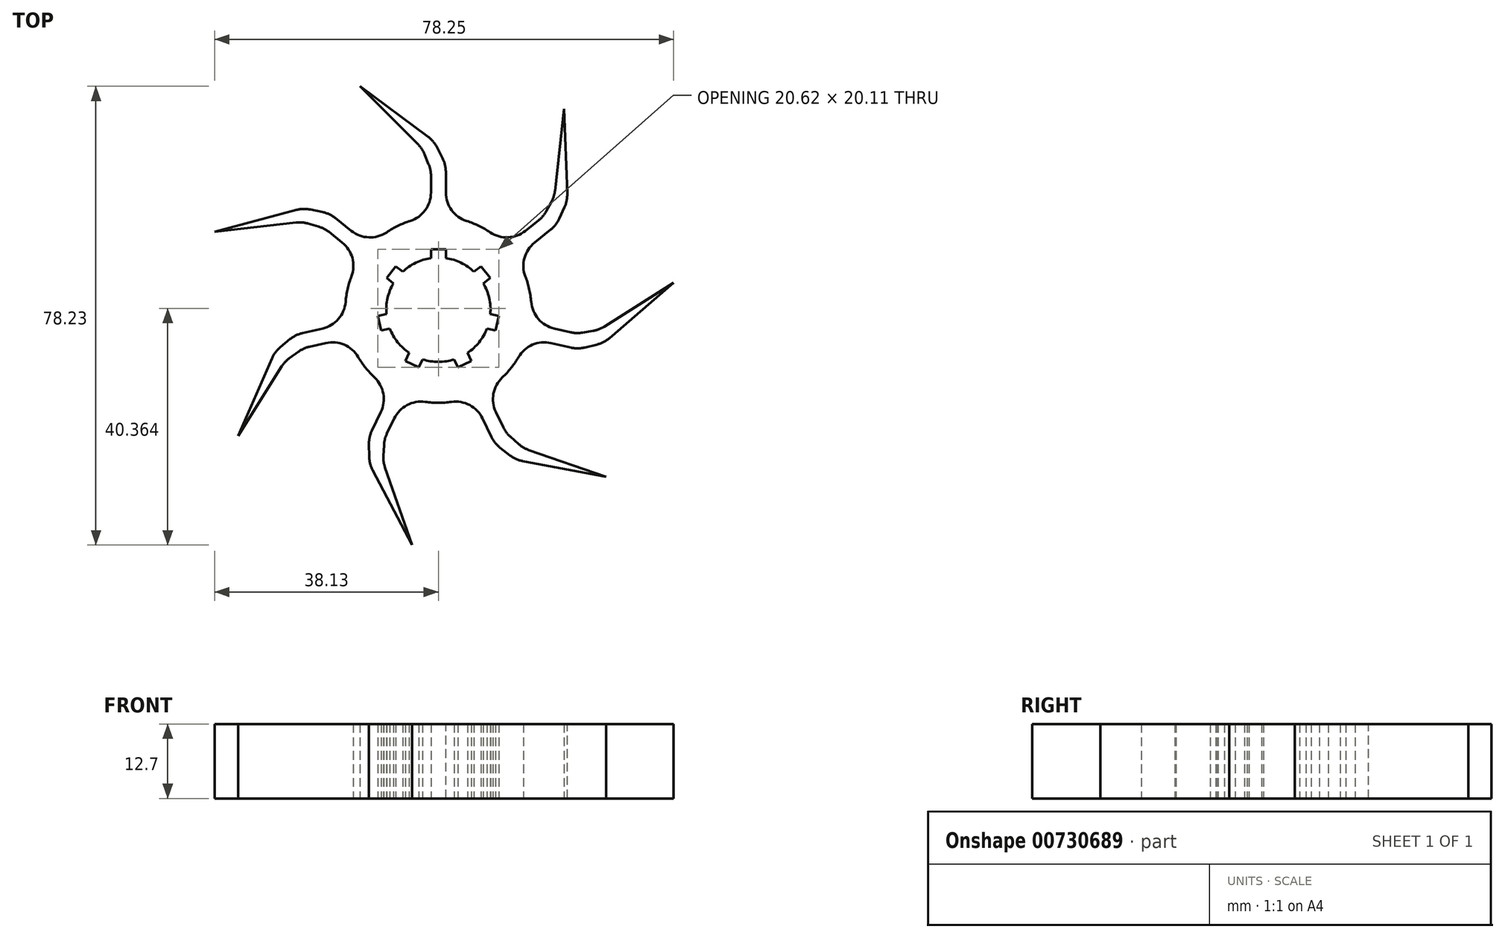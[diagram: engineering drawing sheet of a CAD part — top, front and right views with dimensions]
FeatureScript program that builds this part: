
annotation { "Feature Type Name" : "Feature", "Feature Type Description" : "" }
export const myFeature = defineFeature(function(context is Context, id is Id, definition is map)
    precondition{}
    {
        {
            var Q0;
            Q0=qCreatedBy(makeId("Top.planeOp"),FACE);
            var sketch = newSketch(context, id + "F0", { "sketchPlane" : qUnion([Q0])});
            skCircle(sketch, "E0", {"center": v(0, 0) * mm, "radius": 8.9 * mm});
            skLineSegment(sketch, "E1", {"start": v(-1.27, 8.8) * mm, "end": v(-1.27, 10.29) * mm});
            skLineSegment(sketch, "E2", {"start": v(-1.27, 10.29) * mm, "end": v(1.27, 10.29) * mm});
            skLineSegment(sketch, "E3", {"start": v(1.27, 10.29) * mm, "end": v(1.27, 8.8) * mm});
            skLineSegment(sketch, "E4.1.0", {"start": v(-8.83, 5.42) * mm, "end": v(-7.25, 7.4) * mm});
            skLineSegment(sketch, "E4.1.1", {"start": v(-7.25, 7.4) * mm, "end": v(-6.09, 6.48) * mm});
            skLineSegment(sketch, "E4.1.2", {"start": v(-7.67, 4.5) * mm, "end": v(-8.83, 5.42) * mm});
            skLineSegment(sketch, "E4.2.0", {"start": v(-9.75, -3.53) * mm, "end": v(-10.31, -1.05) * mm});
            skLineSegment(sketch, "E4.2.1", {"start": v(-10.31, -1.05) * mm, "end": v(-8.86, -0.72) * mm});
            skLineSegment(sketch, "E4.2.2", {"start": v(-8.3, -3.2) * mm, "end": v(-9.75, -3.53) * mm});
            skLineSegment(sketch, "E4.3.0", {"start": v(-3.32, -9.82) * mm, "end": v(-5.6, -8.72) * mm});
            skLineSegment(sketch, "E4.3.1", {"start": v(-5.6, -8.72) * mm, "end": v(-4.96, -7.38) * mm});
            skLineSegment(sketch, "E4.3.2", {"start": v(-2.67, -8.48) * mm, "end": v(-3.32, -9.82) * mm});
            skLineSegment(sketch, "E4.4.0", {"start": v(5.6, -8.72) * mm, "end": v(3.32, -9.82) * mm});
            skLineSegment(sketch, "E4.4.1", {"start": v(3.32, -9.82) * mm, "end": v(2.67, -8.48) * mm});
            skLineSegment(sketch, "E4.4.2", {"start": v(4.96, -7.38) * mm, "end": v(5.6, -8.72) * mm});
            skLineSegment(sketch, "E4.5.0", {"start": v(10.31, -1.05) * mm, "end": v(9.75, -3.53) * mm});
            skLineSegment(sketch, "E4.5.1", {"start": v(9.75, -3.53) * mm, "end": v(8.3, -3.2) * mm});
            skLineSegment(sketch, "E4.5.2", {"start": v(8.86, -0.72) * mm, "end": v(10.31, -1.05) * mm});
            skLineSegment(sketch, "E4.6.0", {"start": v(7.25, 7.4) * mm, "end": v(8.83, 5.42) * mm});
            skLineSegment(sketch, "E4.6.1", {"start": v(8.83, 5.42) * mm, "end": v(7.67, 4.5) * mm});
            skLineSegment(sketch, "E4.6.2", {"start": v(6.09, 6.48) * mm, "end": v(7.25, 7.4) * mm});
            skSolve(sketch);
        }
        {
            var Q0;
            Q0=qCreatedBy(makeId("Top.planeOp"),FACE);
            var sketch = newSketch(context, id + "F1", { "sketchPlane" : qUnion([Q0])});
            skCircle(sketch, "E5", {"center": v(0, 0) * mm, "radius": 15.88 * mm});
            skLineSegment(sketch, "E6", {"start": v(-1.27, 15.82) * mm, "end": v(-1.27, 25.98) * mm});
            skLineSegment(sketch, "E7", {"start": v(1.27, 27.25) * mm, "end": v(1.27, 15.82) * mm});
            skLineSegment(sketch, "E8", {"start": v(1.27, 27.25) * mm, "end": v(-13.39, 38.1) * mm});
            skLineSegment(sketch, "E9", {"start": v(-13.39, 38.1) * mm, "end": v(-1.27, 25.98) * mm});
            skLineSegment(sketch, "E10.1.0", {"start": v(-20.52, 17.99) * mm, "end": v(-11.58, 10.86) * mm});
            skLineSegment(sketch, "E10.1.1", {"start": v(-13.16, 8.87) * mm, "end": v(-21.1, 15.2) * mm});
            skLineSegment(sketch, "E10.1.2", {"start": v(-38.13, 13.29) * mm, "end": v(-21.1, 15.2) * mm});
            skLineSegment(sketch, "E10.1.3", {"start": v(-20.52, 17.99) * mm, "end": v(-38.13, 13.29) * mm});
            skLineSegment(sketch, "E10.2.0", {"start": v(-26.85, -4.83) * mm, "end": v(-15.7, -2.28) * mm});
            skLineSegment(sketch, "E10.2.1", {"start": v(-15.14, -4.76) * mm, "end": v(-25.05, -7.02) * mm});
            skLineSegment(sketch, "E10.2.2", {"start": v(-34.17, -21.53) * mm, "end": v(-25.05, -7.02) * mm});
            skLineSegment(sketch, "E10.2.3", {"start": v(-26.85, -4.83) * mm, "end": v(-34.17, -21.53) * mm});
            skLineSegment(sketch, "E10.3.0", {"start": v(-12.97, -24) * mm, "end": v(-8.01, -13.7) * mm});
            skLineSegment(sketch, "E10.3.1", {"start": v(-5.72, -14.8) * mm, "end": v(-10.13, -23.96) * mm});
            skLineSegment(sketch, "E10.3.2", {"start": v(-4.47, -40.13) * mm, "end": v(-10.13, -23.96) * mm});
            skLineSegment(sketch, "E10.3.3", {"start": v(-12.97, -24) * mm, "end": v(-4.47, -40.13) * mm});
            skLineSegment(sketch, "E10.4.0", {"start": v(10.68, -25.1) * mm, "end": v(5.72, -14.8) * mm});
            skLineSegment(sketch, "E10.4.1", {"start": v(8.01, -13.7) * mm, "end": v(12.42, -22.86) * mm});
            skLineSegment(sketch, "E10.4.2", {"start": v(28.6, -28.52) * mm, "end": v(12.42, -22.86) * mm});
            skLineSegment(sketch, "E10.4.3", {"start": v(10.68, -25.1) * mm, "end": v(28.6, -28.52) * mm});
            skLineSegment(sketch, "E10.5.0", {"start": v(26.29, -7.3) * mm, "end": v(15.14, -4.76) * mm});
            skLineSegment(sketch, "E10.5.1", {"start": v(15.7, -2.28) * mm, "end": v(25.62, -4.54) * mm});
            skLineSegment(sketch, "E10.5.2", {"start": v(40.12, 4.57) * mm, "end": v(25.62, -4.54) * mm});
            skLineSegment(sketch, "E10.5.3", {"start": v(26.29, -7.3) * mm, "end": v(40.12, 4.57) * mm});
            skLineSegment(sketch, "E10.6.0", {"start": v(22.1, 16) * mm, "end": v(13.16, 8.87) * mm});
            skLineSegment(sketch, "E10.6.1", {"start": v(11.58, 10.86) * mm, "end": v(19.52, 17.2) * mm});
            skLineSegment(sketch, "E10.6.2", {"start": v(21.44, 34.22) * mm, "end": v(19.52, 17.2) * mm});
            skLineSegment(sketch, "E10.6.3", {"start": v(22.1, 16) * mm, "end": v(21.44, 34.22) * mm});
            skSolve(sketch);
        }
        {
            var Q0;
            {var subQ0=sQuery(id+"F1.wireOp",EDGE,"E5");var subQ8=makeQuery(id+"F1.imprint","INTERSECT",VERTEX,{"derivedFrom":[subQ0,sQuery(id+"F1.wireOp",EDGE,"E10.6.0")]});Q0=makeQuery(id+"F1.imprint","IMPRINT",FACE,{"disambiguationData":[TD([[makeQuery(id+"F1.imprint","IMPRINT",EDGE,{"disambiguationData":[TD([[subQ8,-1.0]])],"derivedFrom":subQ0}),1.0]])]});}
            var Q1;
            {var subQ0=sQuery(id+"F1.wireOp",EDGE,"E10.1.0");Q1=makeQuery(id+"F1.imprint","IMPRINT",FACE,{"disambiguationData":[TD([[makeQuery(id+"F1.imprint","IMPRINT",EDGE,{"derivedFrom":subQ0}),-1.0]])]});}
            var Q2;
            {var subQ1=sQuery(id+"F1.wireOp",EDGE,"E10.2.0");Q2=makeQuery(id+"F1.imprint","IMPRINT",FACE,{"disambiguationData":[TD([[makeQuery(id+"F1.imprint","IMPRINT",EDGE,{"derivedFrom":subQ1}),-1.0]])]});}
            var Q3;
            {var subQ1=sQuery(id+"F1.wireOp",EDGE,"E10.3.0");Q3=makeQuery(id+"F1.imprint","IMPRINT",FACE,{"disambiguationData":[TD([[makeQuery(id+"F1.imprint","IMPRINT",EDGE,{"derivedFrom":subQ1}),-1.0]])]});}
            var Q4;
            {var subQ0=sQuery(id+"F1.wireOp",EDGE,"E10.4.0");Q4=makeQuery(id+"F1.imprint","IMPRINT",FACE,{"disambiguationData":[TD([[makeQuery(id+"F1.imprint","IMPRINT",EDGE,{"derivedFrom":subQ0}),-1.0]])]});}
            var Q5;
            {var subQ1=sQuery(id+"F1.wireOp",EDGE,"E6");Q5=makeQuery(id+"F1.imprint","IMPRINT",FACE,{"disambiguationData":[TD([[makeQuery(id+"F1.imprint","IMPRINT",EDGE,{"derivedFrom":subQ1}),-1.0]])]});}
            var Q6;
            {var subQ1=sQuery(id+"F1.wireOp",EDGE,"E10.6.0");Q6=makeQuery(id+"F1.imprint","IMPRINT",FACE,{"disambiguationData":[TD([[makeQuery(id+"F1.imprint","IMPRINT",EDGE,{"derivedFrom":subQ1}),-1.0]])]});}
            var Q7;
            {var subQ1=sQuery(id+"F1.wireOp",EDGE,"E10.5.0");Q7=makeQuery(id+"F1.imprint","IMPRINT",FACE,{"disambiguationData":[TD([[makeQuery(id+"F1.imprint","IMPRINT",EDGE,{"derivedFrom":subQ1}),-1.0]])]});}
            extrude(context, id + "F2", {"entities" : qUnion([Q0, Q1, Q2, Q3, Q4, Q5, Q6, Q7]), "depth" : 12.7 * mm, "offsetDistance" : 25.4 * mm});
        }
        {
            var Q0;
            Q0 = qSketchRegion(id + "F0", true);
            extrude(context, id + "F3", {"entities" : qUnion([Q0]), "operationType" : NewBodyOperationType.REMOVE, "endBound" : BoundingType.THROUGH_ALL, "depth" : 25.4 * mm, "offsetDistance" : 25.4 * mm});
        }
        {
            var Q0;
            Q0=makeQuery(id+"F2.opExtrude","SWEPT_EDGE",EDGE,{"disambiguationData":[OSD([sQuery(id+"F1.wireOp",EDGE,"E10.1.0"),sQuery(id+"F1.wireOp",EDGE,"E10.1.3")])]});
            var Q1;
            Q1=makeQuery(id+"F2.opExtrude","SWEPT_EDGE",EDGE,{"disambiguationData":[OSD([sQuery(id+"F1.wireOp",EDGE,"E10.1.1"),sQuery(id+"F1.wireOp",EDGE,"E10.1.2")])]});
            var Q2;
            Q2=makeQuery(id+"F2.opExtrude","SWEPT_EDGE",EDGE,{"disambiguationData":[OSD([sQuery(id+"F1.wireOp",EDGE,"E6"),sQuery(id+"F1.wireOp",EDGE,"E9")])]});
            var Q3;
            Q3=makeQuery(id+"F2.opExtrude","SWEPT_EDGE",EDGE,{"disambiguationData":[OSD([sQuery(id+"F1.wireOp",EDGE,"E7"),sQuery(id+"F1.wireOp",EDGE,"E8")])]});
            var Q4;
            Q4=makeQuery(id+"F2.opExtrude","SWEPT_EDGE",EDGE,{"disambiguationData":[OSD([sQuery(id+"F1.wireOp",EDGE,"E10.6.0"),sQuery(id+"F1.wireOp",EDGE,"E10.6.3")])]});
            var Q5;
            Q5=makeQuery(id+"F2.opExtrude","SWEPT_EDGE",EDGE,{"disambiguationData":[OSD([sQuery(id+"F1.wireOp",EDGE,"E10.5.1"),sQuery(id+"F1.wireOp",EDGE,"E10.5.2")])]});
            var Q6;
            Q6=makeQuery(id+"F2.opExtrude","SWEPT_EDGE",EDGE,{"disambiguationData":[OSD([sQuery(id+"F1.wireOp",EDGE,"E10.2.0"),sQuery(id+"F1.wireOp",EDGE,"E10.2.3")])]});
            var Q7;
            Q7=makeQuery(id+"F2.opExtrude","SWEPT_EDGE",EDGE,{"disambiguationData":[OSD([sQuery(id+"F1.wireOp",EDGE,"E10.6.1"),sQuery(id+"F1.wireOp",EDGE,"E10.6.2")])]});
            var Q8;
            Q8=makeQuery(id+"F2.opExtrude","SWEPT_EDGE",EDGE,{"disambiguationData":[OSD([sQuery(id+"F1.wireOp",EDGE,"E10.5.0"),sQuery(id+"F1.wireOp",EDGE,"E10.5.3")])]});
            var Q9;
            Q9=makeQuery(id+"F2.opExtrude","SWEPT_EDGE",EDGE,{"disambiguationData":[OSD([sQuery(id+"F1.wireOp",EDGE,"E10.4.0"),sQuery(id+"F1.wireOp",EDGE,"E10.4.3")])]});
            var Q10;
            Q10=makeQuery(id+"F2.opExtrude","SWEPT_EDGE",EDGE,{"disambiguationData":[OSD([sQuery(id+"F1.wireOp",EDGE,"E10.3.0"),sQuery(id+"F1.wireOp",EDGE,"E10.3.3")])]});
            var Q11;
            Q11=makeQuery(id+"F2.opExtrude","SWEPT_EDGE",EDGE,{"disambiguationData":[OSD([sQuery(id+"F1.wireOp",EDGE,"E10.2.1"),sQuery(id+"F1.wireOp",EDGE,"E10.2.2")])]});
            var Q12;
            Q12=makeQuery(id+"F2.opExtrude","SWEPT_EDGE",EDGE,{"disambiguationData":[OSD([sQuery(id+"F1.wireOp",EDGE,"E10.3.1"),sQuery(id+"F1.wireOp",EDGE,"E10.3.2")])]});
            var Q13;
            Q13=makeQuery(id+"F2.opExtrude","SWEPT_EDGE",EDGE,{"disambiguationData":[OSD([sQuery(id+"F1.wireOp",EDGE,"E10.4.1"),sQuery(id+"F1.wireOp",EDGE,"E10.4.2")])]});
            chamfer(context, id + "F4", {"entities" : qUnion([Q0, Q1, Q2, Q3, Q4, Q5, Q6, Q7, Q8, Q9, Q10, Q11, Q12, Q13]), "width" : 5.08 * mm, "tangentPropagation" : true});
        }
        {
            var Q0;
            {var subQ0=sQuery(id+"F1.wireOp",EDGE,"E10.3.2");Q0=makeQuery(id+"F4.opChamfer","BLEND_EDGE",EDGE,{"blendedFrom":[makeQuery(id+"F2.opExtrude","SWEPT_EDGE",EDGE,{"disambiguationData":[OSD([sQuery(id+"F1.wireOp",EDGE,"E10.3.1"),subQ0])]}),makeQuery(id+"F2.opExtrude","SWEPT_FACE",FACE,{"disambiguationData":[OSD([subQ0])]})],"blendedInto":[makeQuery(id+"F2.opExtrude","SWEPT_FACE",FACE,{"disambiguationData":[OSD([subQ0])]})]});}
            var Q1;
            {var subQ0=sQuery(id+"F1.wireOp",EDGE,"E10.3.1");Q1=makeQuery(id+"F4.opChamfer","BLEND_EDGE",EDGE,{"blendedFrom":[makeQuery(id+"F2.opExtrude","SWEPT_EDGE",EDGE,{"disambiguationData":[OSD([subQ0,sQuery(id+"F1.wireOp",EDGE,"E10.3.2")])]}),makeQuery(id+"F2.opExtrude","SWEPT_FACE",FACE,{"disambiguationData":[OSD([subQ0])]})],"blendedInto":[makeQuery(id+"F2.opExtrude","SWEPT_FACE",FACE,{"disambiguationData":[OSD([subQ0])]})]});}
            var Q2;
            Q2=makeQuery(id+"F2.opExtrude","SWEPT_EDGE",EDGE,{"disambiguationData":[OSD([sQuery(id+"F1.wireOp",EDGE,"E5"),sQuery(id+"F1.wireOp",EDGE,"E10.3.1")])]});
            var Q3;
            Q3=makeQuery(id+"F2.opExtrude","SWEPT_EDGE",EDGE,{"disambiguationData":[OSD([sQuery(id+"F1.wireOp",EDGE,"E5"),sQuery(id+"F1.wireOp",EDGE,"E10.4.1")])]});
            var Q4;
            {var subQ0=sQuery(id+"F1.wireOp",EDGE,"E10.4.1");Q4=makeQuery(id+"F4.opChamfer","BLEND_EDGE",EDGE,{"blendedFrom":[makeQuery(id+"F2.opExtrude","SWEPT_EDGE",EDGE,{"disambiguationData":[OSD([subQ0,sQuery(id+"F1.wireOp",EDGE,"E10.4.2")])]}),makeQuery(id+"F2.opExtrude","SWEPT_FACE",FACE,{"disambiguationData":[OSD([subQ0])]})],"blendedInto":[makeQuery(id+"F2.opExtrude","SWEPT_FACE",FACE,{"disambiguationData":[OSD([subQ0])]})]});}
            var Q5;
            {var subQ0=sQuery(id+"F1.wireOp",EDGE,"E10.4.2");Q5=makeQuery(id+"F4.opChamfer","BLEND_EDGE",EDGE,{"blendedFrom":[makeQuery(id+"F2.opExtrude","SWEPT_EDGE",EDGE,{"disambiguationData":[OSD([sQuery(id+"F1.wireOp",EDGE,"E10.4.1"),subQ0])]}),makeQuery(id+"F2.opExtrude","SWEPT_FACE",FACE,{"disambiguationData":[OSD([subQ0])]})],"blendedInto":[makeQuery(id+"F2.opExtrude","SWEPT_FACE",FACE,{"disambiguationData":[OSD([subQ0])]})]});}
            var Q6;
            Q6=makeQuery(id+"F2.opExtrude","SWEPT_EDGE",EDGE,{"disambiguationData":[OSD([sQuery(id+"F1.wireOp",EDGE,"E5"),sQuery(id+"F1.wireOp",EDGE,"E10.4.0")])]});
            var Q7;
            {var subQ0=sQuery(id+"F1.wireOp",EDGE,"E10.4.0");Q7=makeQuery(id+"F4.opChamfer","BLEND_EDGE",EDGE,{"blendedFrom":[makeQuery(id+"F2.opExtrude","SWEPT_EDGE",EDGE,{"disambiguationData":[OSD([subQ0,sQuery(id+"F1.wireOp",EDGE,"E10.4.3")])]}),makeQuery(id+"F2.opExtrude","SWEPT_FACE",FACE,{"disambiguationData":[OSD([subQ0])]})],"blendedInto":[makeQuery(id+"F2.opExtrude","SWEPT_FACE",FACE,{"disambiguationData":[OSD([subQ0])]})]});}
            var Q8;
            {var subQ0=sQuery(id+"F1.wireOp",EDGE,"E10.4.3");Q8=makeQuery(id+"F4.opChamfer","BLEND_EDGE",EDGE,{"blendedFrom":[makeQuery(id+"F2.opExtrude","SWEPT_EDGE",EDGE,{"disambiguationData":[OSD([sQuery(id+"F1.wireOp",EDGE,"E10.4.0"),subQ0])]}),makeQuery(id+"F2.opExtrude","SWEPT_FACE",FACE,{"disambiguationData":[OSD([subQ0])]})],"blendedInto":[makeQuery(id+"F2.opExtrude","SWEPT_FACE",FACE,{"disambiguationData":[OSD([subQ0])]})]});}
            var Q9;
            {var subQ0=sQuery(id+"F1.wireOp",EDGE,"E10.3.3");Q9=makeQuery(id+"F4.opChamfer","BLEND_EDGE",EDGE,{"blendedFrom":[makeQuery(id+"F2.opExtrude","SWEPT_EDGE",EDGE,{"disambiguationData":[OSD([sQuery(id+"F1.wireOp",EDGE,"E10.3.0"),subQ0])]}),makeQuery(id+"F2.opExtrude","SWEPT_FACE",FACE,{"disambiguationData":[OSD([subQ0])]})],"blendedInto":[makeQuery(id+"F2.opExtrude","SWEPT_FACE",FACE,{"disambiguationData":[OSD([subQ0])]})]});}
            var Q10;
            {var subQ0=sQuery(id+"F1.wireOp",EDGE,"E10.3.0");Q10=makeQuery(id+"F4.opChamfer","BLEND_EDGE",EDGE,{"blendedFrom":[makeQuery(id+"F2.opExtrude","SWEPT_EDGE",EDGE,{"disambiguationData":[OSD([subQ0,sQuery(id+"F1.wireOp",EDGE,"E10.3.3")])]}),makeQuery(id+"F2.opExtrude","SWEPT_FACE",FACE,{"disambiguationData":[OSD([subQ0])]})],"blendedInto":[makeQuery(id+"F2.opExtrude","SWEPT_FACE",FACE,{"disambiguationData":[OSD([subQ0])]})]});}
            var Q11;
            Q11=makeQuery(id+"F2.opExtrude","SWEPT_EDGE",EDGE,{"disambiguationData":[OSD([sQuery(id+"F1.wireOp",EDGE,"E5"),sQuery(id+"F1.wireOp",EDGE,"E10.3.0")])]});
            var Q12;
            Q12=makeQuery(id+"F2.opExtrude","SWEPT_EDGE",EDGE,{"disambiguationData":[OSD([sQuery(id+"F1.wireOp",EDGE,"E5"),sQuery(id+"F1.wireOp",EDGE,"E10.5.0")])]});
            var Q13;
            {var subQ0=sQuery(id+"F1.wireOp",EDGE,"E10.5.0");Q13=makeQuery(id+"F4.opChamfer","BLEND_EDGE",EDGE,{"blendedFrom":[makeQuery(id+"F2.opExtrude","SWEPT_EDGE",EDGE,{"disambiguationData":[OSD([subQ0,sQuery(id+"F1.wireOp",EDGE,"E10.5.3")])]}),makeQuery(id+"F2.opExtrude","SWEPT_FACE",FACE,{"disambiguationData":[OSD([subQ0])]})],"blendedInto":[makeQuery(id+"F2.opExtrude","SWEPT_FACE",FACE,{"disambiguationData":[OSD([subQ0])]})]});}
            var Q14;
            {var subQ0=sQuery(id+"F1.wireOp",EDGE,"E10.5.3");Q14=makeQuery(id+"F4.opChamfer","BLEND_EDGE",EDGE,{"blendedFrom":[makeQuery(id+"F2.opExtrude","SWEPT_EDGE",EDGE,{"disambiguationData":[OSD([sQuery(id+"F1.wireOp",EDGE,"E10.5.0"),subQ0])]}),makeQuery(id+"F2.opExtrude","SWEPT_FACE",FACE,{"disambiguationData":[OSD([subQ0])]})],"blendedInto":[makeQuery(id+"F2.opExtrude","SWEPT_FACE",FACE,{"disambiguationData":[OSD([subQ0])]})]});}
            var Q15;
            Q15=makeQuery(id+"F2.opExtrude","SWEPT_EDGE",EDGE,{"disambiguationData":[OSD([sQuery(id+"F1.wireOp",EDGE,"E5"),sQuery(id+"F1.wireOp",EDGE,"E10.5.1")])]});
            var Q16;
            {var subQ0=sQuery(id+"F1.wireOp",EDGE,"E10.5.2");Q16=makeQuery(id+"F4.opChamfer","BLEND_EDGE",EDGE,{"blendedFrom":[makeQuery(id+"F2.opExtrude","SWEPT_EDGE",EDGE,{"disambiguationData":[OSD([sQuery(id+"F1.wireOp",EDGE,"E10.5.1"),subQ0])]}),makeQuery(id+"F2.opExtrude","SWEPT_FACE",FACE,{"disambiguationData":[OSD([subQ0])]})],"blendedInto":[makeQuery(id+"F2.opExtrude","SWEPT_FACE",FACE,{"disambiguationData":[OSD([subQ0])]})]});}
            var Q17;
            {var subQ0=sQuery(id+"F1.wireOp",EDGE,"E10.5.1");Q17=makeQuery(id+"F4.opChamfer","BLEND_EDGE",EDGE,{"blendedFrom":[makeQuery(id+"F2.opExtrude","SWEPT_EDGE",EDGE,{"disambiguationData":[OSD([subQ0,sQuery(id+"F1.wireOp",EDGE,"E10.5.2")])]}),makeQuery(id+"F2.opExtrude","SWEPT_FACE",FACE,{"disambiguationData":[OSD([subQ0])]})],"blendedInto":[makeQuery(id+"F2.opExtrude","SWEPT_FACE",FACE,{"disambiguationData":[OSD([subQ0])]})]});}
            var Q18;
            Q18=makeQuery(id+"F2.opExtrude","SWEPT_EDGE",EDGE,{"disambiguationData":[OSD([sQuery(id+"F1.wireOp",EDGE,"E5"),sQuery(id+"F1.wireOp",EDGE,"E10.6.0")])]});
            var Q19;
            {var subQ0=sQuery(id+"F1.wireOp",EDGE,"E10.6.0");Q19=makeQuery(id+"F4.opChamfer","BLEND_EDGE",EDGE,{"blendedFrom":[makeQuery(id+"F2.opExtrude","SWEPT_EDGE",EDGE,{"disambiguationData":[OSD([subQ0,sQuery(id+"F1.wireOp",EDGE,"E10.6.3")])]}),makeQuery(id+"F2.opExtrude","SWEPT_FACE",FACE,{"disambiguationData":[OSD([subQ0])]})],"blendedInto":[makeQuery(id+"F2.opExtrude","SWEPT_FACE",FACE,{"disambiguationData":[OSD([subQ0])]})]});}
            var Q20;
            {var subQ0=sQuery(id+"F1.wireOp",EDGE,"E10.6.3");Q20=makeQuery(id+"F4.opChamfer","BLEND_EDGE",EDGE,{"blendedFrom":[makeQuery(id+"F2.opExtrude","SWEPT_EDGE",EDGE,{"disambiguationData":[OSD([sQuery(id+"F1.wireOp",EDGE,"E10.6.0"),subQ0])]}),makeQuery(id+"F2.opExtrude","SWEPT_FACE",FACE,{"disambiguationData":[OSD([subQ0])]})],"blendedInto":[makeQuery(id+"F2.opExtrude","SWEPT_FACE",FACE,{"disambiguationData":[OSD([subQ0])]})]});}
            var Q21;
            Q21=makeQuery(id+"F2.opExtrude","SWEPT_EDGE",EDGE,{"disambiguationData":[OSD([sQuery(id+"F1.wireOp",EDGE,"E5"),sQuery(id+"F1.wireOp",EDGE,"E10.6.1")])]});
            var Q22;
            {var subQ0=sQuery(id+"F1.wireOp",EDGE,"E10.6.1");Q22=makeQuery(id+"F4.opChamfer","BLEND_EDGE",EDGE,{"blendedFrom":[makeQuery(id+"F2.opExtrude","SWEPT_EDGE",EDGE,{"disambiguationData":[OSD([subQ0,sQuery(id+"F1.wireOp",EDGE,"E10.6.2")])]}),makeQuery(id+"F2.opExtrude","SWEPT_FACE",FACE,{"disambiguationData":[OSD([subQ0])]})],"blendedInto":[makeQuery(id+"F2.opExtrude","SWEPT_FACE",FACE,{"disambiguationData":[OSD([subQ0])]})]});}
            var Q23;
            {var subQ0=sQuery(id+"F1.wireOp",EDGE,"E10.6.2");Q23=makeQuery(id+"F4.opChamfer","BLEND_EDGE",EDGE,{"blendedFrom":[makeQuery(id+"F2.opExtrude","SWEPT_EDGE",EDGE,{"disambiguationData":[OSD([sQuery(id+"F1.wireOp",EDGE,"E10.6.1"),subQ0])]}),makeQuery(id+"F2.opExtrude","SWEPT_FACE",FACE,{"disambiguationData":[OSD([subQ0])]})],"blendedInto":[makeQuery(id+"F2.opExtrude","SWEPT_FACE",FACE,{"disambiguationData":[OSD([subQ0])]})]});}
            var Q24;
            Q24=makeQuery(id+"F2.opExtrude","SWEPT_EDGE",EDGE,{"disambiguationData":[OSD([sQuery(id+"F1.wireOp",EDGE,"E5"),sQuery(id+"F1.wireOp",EDGE,"E7")])]});
            var Q25;
            {var subQ0=sQuery(id+"F1.wireOp",EDGE,"E7");Q25=makeQuery(id+"F4.opChamfer","BLEND_EDGE",EDGE,{"blendedFrom":[makeQuery(id+"F2.opExtrude","SWEPT_EDGE",EDGE,{"disambiguationData":[OSD([subQ0,sQuery(id+"F1.wireOp",EDGE,"E8")])]}),makeQuery(id+"F2.opExtrude","SWEPT_FACE",FACE,{"disambiguationData":[OSD([subQ0])]})],"blendedInto":[makeQuery(id+"F2.opExtrude","SWEPT_FACE",FACE,{"disambiguationData":[OSD([subQ0])]})]});}
            var Q26;
            {var subQ0=sQuery(id+"F1.wireOp",EDGE,"E8");Q26=makeQuery(id+"F4.opChamfer","BLEND_EDGE",EDGE,{"blendedFrom":[makeQuery(id+"F2.opExtrude","SWEPT_EDGE",EDGE,{"disambiguationData":[OSD([sQuery(id+"F1.wireOp",EDGE,"E7"),subQ0])]}),makeQuery(id+"F2.opExtrude","SWEPT_FACE",FACE,{"disambiguationData":[OSD([subQ0])]})],"blendedInto":[makeQuery(id+"F2.opExtrude","SWEPT_FACE",FACE,{"disambiguationData":[OSD([subQ0])]})]});}
            var Q27;
            {var subQ0=sQuery(id+"F1.wireOp",EDGE,"E9");Q27=makeQuery(id+"F4.opChamfer","BLEND_EDGE",EDGE,{"blendedFrom":[makeQuery(id+"F2.opExtrude","SWEPT_EDGE",EDGE,{"disambiguationData":[OSD([sQuery(id+"F1.wireOp",EDGE,"E6"),subQ0])]}),makeQuery(id+"F2.opExtrude","SWEPT_FACE",FACE,{"disambiguationData":[OSD([subQ0])]})],"blendedInto":[makeQuery(id+"F2.opExtrude","SWEPT_FACE",FACE,{"disambiguationData":[OSD([subQ0])]})]});}
            var Q28;
            {var subQ0=sQuery(id+"F1.wireOp",EDGE,"E6");Q28=makeQuery(id+"F4.opChamfer","BLEND_EDGE",EDGE,{"blendedFrom":[makeQuery(id+"F2.opExtrude","SWEPT_EDGE",EDGE,{"disambiguationData":[OSD([subQ0,sQuery(id+"F1.wireOp",EDGE,"E9")])]}),makeQuery(id+"F2.opExtrude","SWEPT_FACE",FACE,{"disambiguationData":[OSD([subQ0])]})],"blendedInto":[makeQuery(id+"F2.opExtrude","SWEPT_FACE",FACE,{"disambiguationData":[OSD([subQ0])]})]});}
            var Q29;
            Q29=makeQuery(id+"F2.opExtrude","SWEPT_EDGE",EDGE,{"disambiguationData":[OSD([sQuery(id+"F1.wireOp",EDGE,"E5"),sQuery(id+"F1.wireOp",EDGE,"E6")])]});
            var Q30;
            {var subQ0=sQuery(id+"F1.wireOp",EDGE,"E10.2.3");Q30=makeQuery(id+"F4.opChamfer","BLEND_EDGE",EDGE,{"blendedFrom":[makeQuery(id+"F2.opExtrude","SWEPT_EDGE",EDGE,{"disambiguationData":[OSD([sQuery(id+"F1.wireOp",EDGE,"E10.2.0"),subQ0])]}),makeQuery(id+"F2.opExtrude","SWEPT_FACE",FACE,{"disambiguationData":[OSD([subQ0])]})],"blendedInto":[makeQuery(id+"F2.opExtrude","SWEPT_FACE",FACE,{"disambiguationData":[OSD([subQ0])]})]});}
            var Q31;
            {var subQ0=sQuery(id+"F1.wireOp",EDGE,"E10.2.0");Q31=makeQuery(id+"F4.opChamfer","BLEND_EDGE",EDGE,{"blendedFrom":[makeQuery(id+"F2.opExtrude","SWEPT_EDGE",EDGE,{"disambiguationData":[OSD([subQ0,sQuery(id+"F1.wireOp",EDGE,"E10.2.3")])]}),makeQuery(id+"F2.opExtrude","SWEPT_FACE",FACE,{"disambiguationData":[OSD([subQ0])]})],"blendedInto":[makeQuery(id+"F2.opExtrude","SWEPT_FACE",FACE,{"disambiguationData":[OSD([subQ0])]})]});}
            var Q32;
            Q32=makeQuery(id+"F2.opExtrude","SWEPT_EDGE",EDGE,{"disambiguationData":[OSD([sQuery(id+"F1.wireOp",EDGE,"E5"),sQuery(id+"F1.wireOp",EDGE,"E10.2.0")])]});
            var Q33;
            Q33=makeQuery(id+"F2.opExtrude","SWEPT_EDGE",EDGE,{"disambiguationData":[OSD([sQuery(id+"F1.wireOp",EDGE,"E5"),sQuery(id+"F1.wireOp",EDGE,"E10.1.1")])]});
            var Q34;
            {var subQ0=sQuery(id+"F1.wireOp",EDGE,"E10.1.1");Q34=makeQuery(id+"F4.opChamfer","BLEND_EDGE",EDGE,{"blendedFrom":[makeQuery(id+"F2.opExtrude","SWEPT_EDGE",EDGE,{"disambiguationData":[OSD([subQ0,sQuery(id+"F1.wireOp",EDGE,"E10.1.2")])]}),makeQuery(id+"F2.opExtrude","SWEPT_FACE",FACE,{"disambiguationData":[OSD([subQ0])]})],"blendedInto":[makeQuery(id+"F2.opExtrude","SWEPT_FACE",FACE,{"disambiguationData":[OSD([subQ0])]})]});}
            var Q35;
            {var subQ0=sQuery(id+"F1.wireOp",EDGE,"E10.1.2");Q35=makeQuery(id+"F4.opChamfer","BLEND_EDGE",EDGE,{"blendedFrom":[makeQuery(id+"F2.opExtrude","SWEPT_EDGE",EDGE,{"disambiguationData":[OSD([sQuery(id+"F1.wireOp",EDGE,"E10.1.1"),subQ0])]}),makeQuery(id+"F2.opExtrude","SWEPT_FACE",FACE,{"disambiguationData":[OSD([subQ0])]})],"blendedInto":[makeQuery(id+"F2.opExtrude","SWEPT_FACE",FACE,{"disambiguationData":[OSD([subQ0])]})]});}
            var Q36;
            {var subQ0=sQuery(id+"F1.wireOp",EDGE,"E10.1.0");Q36=makeQuery(id+"F4.opChamfer","BLEND_EDGE",EDGE,{"blendedFrom":[makeQuery(id+"F2.opExtrude","SWEPT_EDGE",EDGE,{"disambiguationData":[OSD([subQ0,sQuery(id+"F1.wireOp",EDGE,"E10.1.3")])]}),makeQuery(id+"F2.opExtrude","SWEPT_FACE",FACE,{"disambiguationData":[OSD([subQ0])]})],"blendedInto":[makeQuery(id+"F2.opExtrude","SWEPT_FACE",FACE,{"disambiguationData":[OSD([subQ0])]})]});}
            var Q37;
            {var subQ0=sQuery(id+"F1.wireOp",EDGE,"E10.1.3");Q37=makeQuery(id+"F4.opChamfer","BLEND_EDGE",EDGE,{"blendedFrom":[makeQuery(id+"F2.opExtrude","SWEPT_EDGE",EDGE,{"disambiguationData":[OSD([sQuery(id+"F1.wireOp",EDGE,"E10.1.0"),subQ0])]}),makeQuery(id+"F2.opExtrude","SWEPT_FACE",FACE,{"disambiguationData":[OSD([subQ0])]})],"blendedInto":[makeQuery(id+"F2.opExtrude","SWEPT_FACE",FACE,{"disambiguationData":[OSD([subQ0])]})]});}
            var Q38;
            Q38=makeQuery(id+"F2.opExtrude","SWEPT_EDGE",EDGE,{"disambiguationData":[OSD([sQuery(id+"F1.wireOp",EDGE,"E5"),sQuery(id+"F1.wireOp",EDGE,"E10.1.0")])]});
            var Q39;
            Q39=makeQuery(id+"F2.opExtrude","SWEPT_EDGE",EDGE,{"disambiguationData":[OSD([sQuery(id+"F1.wireOp",EDGE,"E5"),sQuery(id+"F1.wireOp",EDGE,"E10.2.1")])]});
            var Q40;
            {var subQ0=sQuery(id+"F1.wireOp",EDGE,"E10.2.1");Q40=makeQuery(id+"F4.opChamfer","BLEND_EDGE",EDGE,{"blendedFrom":[makeQuery(id+"F2.opExtrude","SWEPT_EDGE",EDGE,{"disambiguationData":[OSD([subQ0,sQuery(id+"F1.wireOp",EDGE,"E10.2.2")])]}),makeQuery(id+"F2.opExtrude","SWEPT_FACE",FACE,{"disambiguationData":[OSD([subQ0])]})],"blendedInto":[makeQuery(id+"F2.opExtrude","SWEPT_FACE",FACE,{"disambiguationData":[OSD([subQ0])]})]});}
            var Q41;
            {var subQ0=sQuery(id+"F1.wireOp",EDGE,"E10.2.2");Q41=makeQuery(id+"F4.opChamfer","BLEND_EDGE",EDGE,{"blendedFrom":[makeQuery(id+"F2.opExtrude","SWEPT_EDGE",EDGE,{"disambiguationData":[OSD([sQuery(id+"F1.wireOp",EDGE,"E10.2.1"),subQ0])]}),makeQuery(id+"F2.opExtrude","SWEPT_FACE",FACE,{"disambiguationData":[OSD([subQ0])]})],"blendedInto":[makeQuery(id+"F2.opExtrude","SWEPT_FACE",FACE,{"disambiguationData":[OSD([subQ0])]})]});}
            fillet(context, id + "F5", {"entities" : qUnion([Q0, Q1, Q2, Q3, Q4, Q5, Q6, Q7, Q8, Q9, Q10, Q11, Q12, Q13, Q14, Q15, Q16, Q17, Q18, Q19, Q20, Q21, Q22, Q23, Q24, Q25, Q26, Q27, Q28, Q29, Q30, Q31, Q32, Q33, Q34, Q35, Q36, Q37, Q38, Q39, Q40, Q41]), "radius" : 5.08 * mm, "tangentPropagation" : true, "allowEdgeOverflow" : false});
        }
    });
